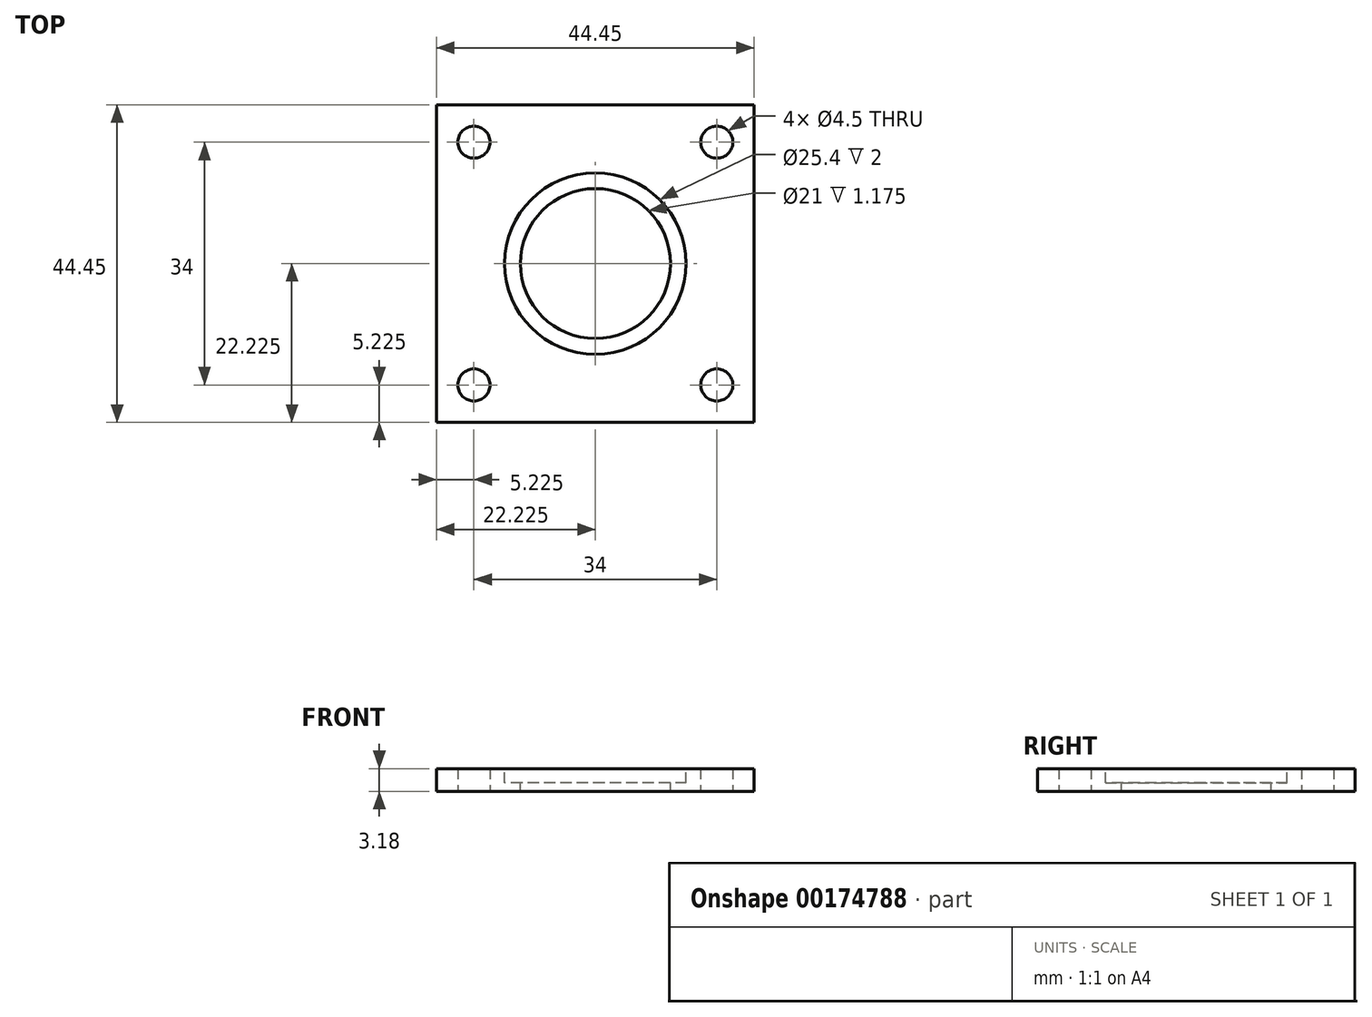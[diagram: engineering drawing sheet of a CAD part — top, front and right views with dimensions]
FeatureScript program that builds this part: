
annotation { "Feature Type Name" : "Feature", "Feature Type Description" : "" }
export const myFeature = defineFeature(function(context is Context, id is Id, definition is map)
    precondition{}
    {
        {
            var Q0;
            Q0=qCreatedBy(makeId("Top.planeOp"),FACE);
            var sketch = newSketch(context, id + "F0", { "sketchPlane" : qUnion([Q0])});
            skLineSegment(sketch, "E0.bottom", {"start": v(0, 0) * mm, "end": v(44.45, 0) * mm});
            skLineSegment(sketch, "E0.top", {"start": v(0, 44.45) * mm, "end": v(44.45, 44.45) * mm});
            skLineSegment(sketch, "E0.left", {"start": v(0, 0) * mm, "end": v(0, 44.45) * mm});
            skLineSegment(sketch, "E0.right", {"start": v(44.45, 0) * mm, "end": v(44.45, 44.45) * mm});
            skLineSegment(sketch, "E1.bottom", {"start": v(5.23, 39.23) * mm, "end": v(39.23, 39.23) * mm});
            skLineSegment(sketch, "E1.top", {"start": v(5.23, 5.23) * mm, "end": v(39.23, 5.23) * mm});
            skLineSegment(sketch, "E1.left", {"start": v(5.23, 39.23) * mm, "end": v(5.23, 5.23) * mm});
            skLineSegment(sketch, "E1.right", {"start": v(39.23, 39.23) * mm, "end": v(39.23, 5.23) * mm});
            skLineSegment(sketch, "E2", {"start": v(5.23, 39.23) * mm, "end": v(0, 39.23) * mm});
            skLineSegment(sketch, "E3", {"start": v(5.23, 39.23) * mm, "end": v(5.23, 44.45) * mm});
            skLineSegment(sketch, "E4", {"start": v(39.23, 5.23) * mm, "end": v(39.23, 0) * mm});
            skLineSegment(sketch, "E5", {"start": v(39.23, 5.23) * mm, "end": v(44.45, 5.23) * mm});
            skSolve(sketch);
        }
        {
            var Q0;
            Q0 = qSketchRegion(id + "F0", true);
            var Q1;
            Q1=makeQuery(id+"F0.imprint","IMPRINT",FACE,{"disambiguationData":[TD([[makeQuery(id+"F0.imprint","IMPRINT",EDGE,{"derivedFrom":sQuery(id+"F0.wireOp",EDGE,"E1.bottom")}),-1.0]])]});
            extrude(context, id + "F1", {"entities" : qUnion([Q0, Q1]), "depth" : 3.17 * mm});
        }
        {
            var Q0;
            Q0=sQuery(id+"F0.wireOp",VERTEX,"E1.left.start");
            var Q1;
            Q1=sQuery(id+"F0.wireOp",VERTEX,"E1.right.start");
            var Q2;
            Q2=sQuery(id+"F0.wireOp",VERTEX,"E1.right.end");
            var Q3;
            Q3=sQuery(id+"F0.wireOp",VERTEX,"E1.left.end");
            var Q4;
            Q4=makeQuery(id+"F1.opExtrude","SWEPT_BODY",BODY,{"disambiguationData":[OSD([sQuery(id+"F0.wireOp",EDGE,"E0.bottom"),sQuery(id+"F0.wireOp",EDGE,"E0.top"),sQuery(id+"F0.wireOp",EDGE,"E0.left"),sQuery(id+"F0.wireOp",EDGE,"E0.right")])]});
            hole(context, id + "F2", {"style" : HoleStyle.SIMPLE, "endStyle" : HoleEndStyle.BLIND, "oppositeDirection" : true, "standardTappedOrClearance" : lookupTablePath({ "standard" : "ANSI", "fit" : "Normal (ASME)", "size" : "#8", "type" : "Clearance" }), "standardBlindInLast" : lookupTablePath({ "fit" : "Free", "standard" : "ANSI", "size" : "#8", "type" : "Clearance" }), "holeDiameter" : 4.5 * mm, "holeDepth" : 45.72 * mm, "locations" : qUnion([Q0, Q1, Q2, Q3]), "scope" : qUnion([Q4])});
        }
        {
            var Q0;
            Q0=makeQuery(id+"F1.opExtrude","CAP_FACE",FACE,{"disambiguationData":[OSD([sQuery(id+"F0.wireOp",EDGE,"E0.bottom"),sQuery(id+"F0.wireOp",EDGE,"E0.top"),sQuery(id+"F0.wireOp",EDGE,"E0.left"),sQuery(id+"F0.wireOp",EDGE,"E0.right")])],"isStart":false});
            var sketch = newSketch(context, id + "F3", { "sketchPlane" : qUnion([Q0])});
            skLineSegment(sketch, "E6", {"start": v(22.23, 44.45) * mm, "end": v(22.23, 0) * mm});
            skLineSegment(sketch, "E7", {"start": v(44.45, 22.23) * mm, "end": v(0, 22.23) * mm});
            skCircle(sketch, "E8", {"center": v(22.23, 22.23) * mm, "radius": 12.7 * mm});
            skSolve(sketch);
        }
        {
            var Q0;
            Q0 = qSketchRegion(id + "F3", true);
            extrude(context, id + "F4", {"entities" : qUnion([Q0]), "operationType" : NewBodyOperationType.REMOVE, "oppositeDirection" : true, "depth" : 2 * mm});
        }
        {
            var Q0;
            Q0=makeQuery(id+"F4.boolean.opBoolean","COPY",FACE,{"derivedFrom":makeQuery(id+"F4.opExtrude","CAP_FACE",FACE,{"disambiguationData":[OSD([sQuery(id+"F3.wireOp",EDGE,"E8")])],"isStart":false})});
            var sketch = newSketch(context, id + "F5", { "sketchPlane" : qUnion([Q0])});
            skCircle(sketch, "E9", {"center": v(22.23, 22.23) * mm, "radius": 10.5 * mm});
            skSolve(sketch);
        }
        {
            var Q0;
            Q0 = qSketchRegion(id + "F5", true);
            extrude(context, id + "F6", {"entities" : qUnion([Q0]), "operationType" : NewBodyOperationType.REMOVE, "endBound" : BoundingType.THROUGH_ALL, "oppositeDirection" : true, "depth" : 25.4 * mm});
        }
    });
